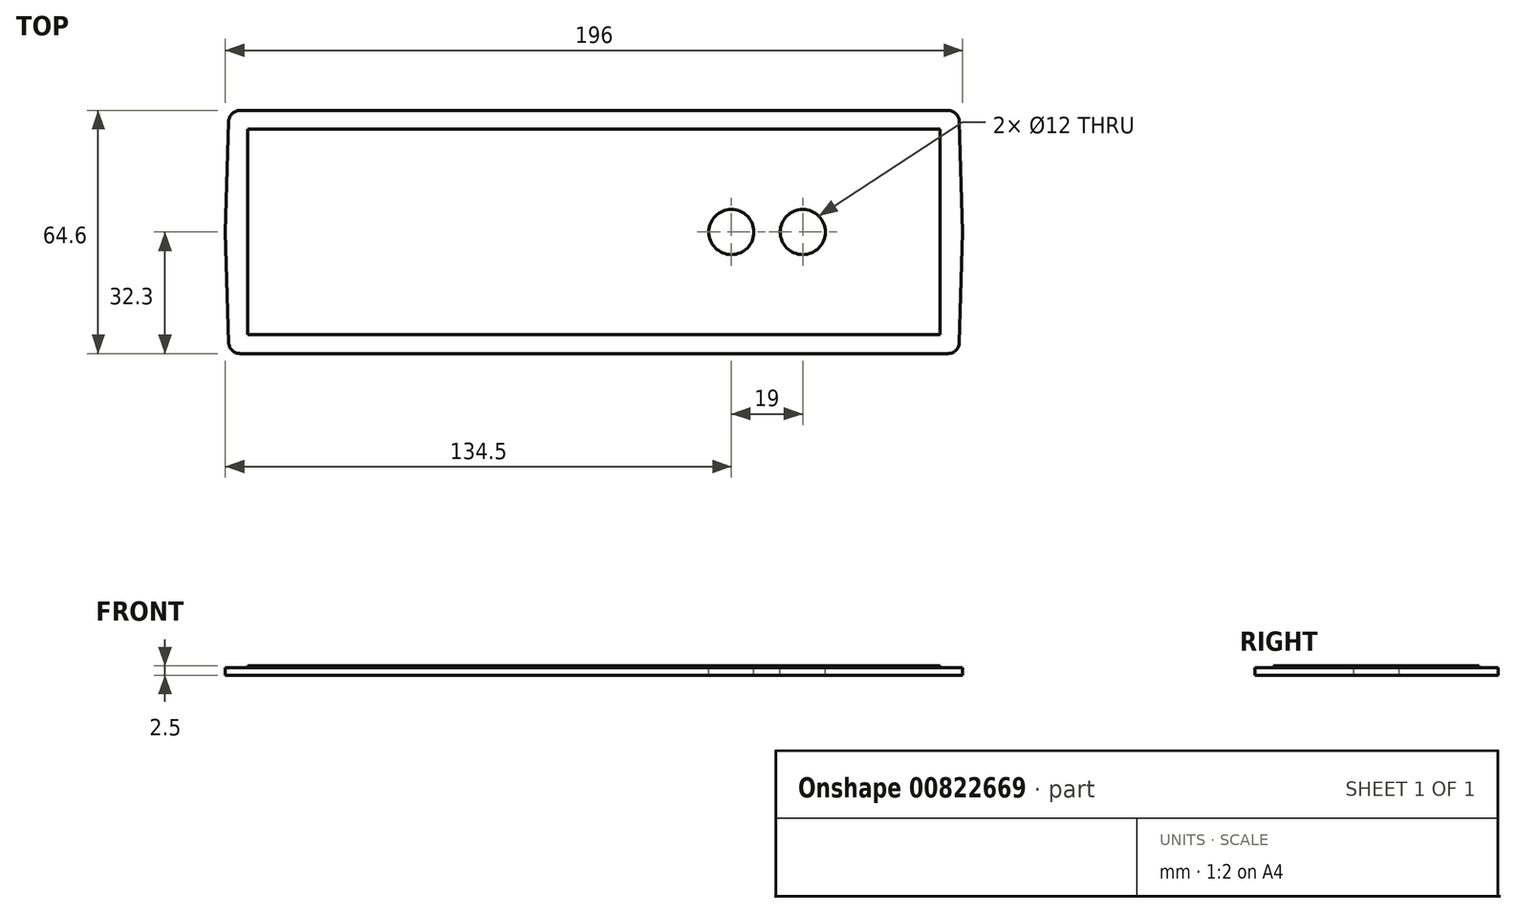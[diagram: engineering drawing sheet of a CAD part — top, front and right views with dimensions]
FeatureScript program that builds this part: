
annotation { "Feature Type Name" : "Feature", "Feature Type Description" : "" }
export const myFeature = defineFeature(function(context is Context, id is Id, definition is map)
    precondition{}
    {
        {
            var Q0;
            Q0=qCreatedBy(makeId("Top.planeOp"),FACE);
            var sketch = newSketch(context, id + "F0", { "sketchPlane" : qUnion([Q0])});
            skLineSegment(sketch, "E0.bottom", {"start": v(97, 32.3) * mm, "end": v(-97, 32.3) * mm});
            skLineSegment(sketch, "E0.top", {"start": v(97, -32.3) * mm, "end": v(-97, -32.3) * mm});
            skLineSegment(sketch, "E0.left", {"start": v(97, 32.3) * mm, "end": v(97, -32.3) * mm});
            skLineSegment(sketch, "E0.right", {"start": v(-97, 32.3) * mm, "end": v(-97, -32.3) * mm});
            skPoint(sketch, "E0.middle", {"position": v(0, 0) * mm});
            skLineSegment(sketch, "E1", {"start": v(98, 0) * mm, "end": v(97, -32.3) * mm});
            skPoint(sketch, "E1.startSnap0", {"position": v(97, 0) * mm});
            skLineSegment(sketch, "E2", {"start": v(98, 0) * mm, "end": v(97, 32.3) * mm});
            skLineSegment(sketch, "E3", {"start": v(-98, 0) * mm, "end": v(-97, 32.3) * mm});
            skLineSegment(sketch, "E4", {"start": v(-98, 0) * mm, "end": v(-97, -32.3) * mm});
            skSolve(sketch);
        }
        {
            var Q0;
            Q0=makeQuery(id+"F0.imprint","IMPRINT",FACE,{"disambiguationData":[TD([[makeQuery(id+"F0.imprint","IMPRINT",EDGE,{"derivedFrom":sQuery(id+"F0.wireOp",EDGE,"E0.bottom")}),1.0]])]});
            var Q1;
            Q1=makeQuery(id+"F0.imprint","IMPRINT",FACE,{"disambiguationData":[TD([[makeQuery(id+"F0.imprint","IMPRINT",EDGE,{"derivedFrom":sQuery(id+"F0.wireOp",EDGE,"E0.left")}),1.0]])]});
            var Q2;
            Q2=makeQuery(id+"F0.imprint","IMPRINT",FACE,{"disambiguationData":[TD([[makeQuery(id+"F0.imprint","IMPRINT",EDGE,{"derivedFrom":sQuery(id+"F0.wireOp",EDGE,"E0.right")}),-1.0]])]});
            extrude(context, id + "F1", {"entities" : qUnion([Q0, Q1, Q2]), "depth" : 2 * mm, "offsetDistance" : 25 * mm});
        }
        {
            var Q0;
            Q0=makeQuery(id+"F1.opExtrude","CAP_FACE",FACE,{"disambiguationData":[OSD([sQuery(id+"F0.wireOp",EDGE,"E0.bottom"),sQuery(id+"F0.wireOp",EDGE,"E0.top"),sQuery(id+"F0.wireOp",EDGE,"E0.left"),sQuery(id+"F0.wireOp",EDGE,"E0.right")])],"isStart":false});
            var sketch = newSketch(context, id + "F2", { "sketchPlane" : qUnion([Q0])});
            skLineSegment(sketch, "E5.bottom", {"start": v(92, 27.3) * mm, "end": v(-92, 27.3) * mm});
            skLineSegment(sketch, "E5.top", {"start": v(92, -27.3) * mm, "end": v(-92, -27.3) * mm});
            skLineSegment(sketch, "E5.left", {"start": v(92, 27.3) * mm, "end": v(92, -27.3) * mm});
            skLineSegment(sketch, "E5.right", {"start": v(-92, 27.3) * mm, "end": v(-92, -27.3) * mm});
            skPoint(sketch, "E5.middle", {"position": v(0, 0) * mm});
            skSolve(sketch);
        }
        {
            var Q0;
            Q0=makeQuery(id+"F2.imprint","IMPRINT",FACE,{"disambiguationData":[TD([[makeQuery(id+"F2.imprint","IMPRINT",EDGE,{"derivedFrom":sQuery(id+"F2.wireOp",EDGE,"E5.bottom")}),1.0]])]});
            extrude(context, id + "F3", {"entities" : qUnion([Q0]), "operationType" : NewBodyOperationType.ADD, "depth" : .5 * mm, "offsetDistance" : 25 * mm});
        }
        {
            var Q0;
            Q0=makeQuery(id+"F3.opExtrude","CAP_FACE",FACE,{"disambiguationData":[OSD([sQuery(id+"F2.wireOp",EDGE,"E5.bottom"),sQuery(id+"F2.wireOp",EDGE,"E5.top"),sQuery(id+"F2.wireOp",EDGE,"E5.left"),sQuery(id+"F2.wireOp",EDGE,"E5.right")])],"isStart":false});
            var sketch = newSketch(context, id + "F4", { "sketchPlane" : qUnion([Q0])});
            skLineSegment(sketch, "E6.bottom", {"start": v(-81.75, 19.75) * mm, "end": v(-10.25, 19.75) * mm});
            skLineSegment(sketch, "E6.top", {"start": v(-81.75, -19.75) * mm, "end": v(-10.25, -19.75) * mm});
            skLineSegment(sketch, "E6.left", {"start": v(-81.75, 19.75) * mm, "end": v(-81.75, -19.75) * mm});
            skLineSegment(sketch, "E6.right", {"start": v(-10.25, 19.75) * mm, "end": v(-10.25, -19.75) * mm});
            skLineSegment(sketch, "E7", {"start": v(-81.75, 19.75) * mm, "end": v(-81.75, 27.3) * mm, "construction": true});
            skLineSegment(sketch, "E8", {"start": v(-81.75, -19.75) * mm, "end": v(-81.75, -27.3) * mm, "construction": true});
            skLineSegment(sketch, "E9", {"start": v(-81.75, 19.75) * mm, "end": v(-92, 19.75) * mm, "construction": true});
            skLineSegment(sketch, "E10", {"start": v(-10.25, 19.75) * mm, "end": v(0, 19.75) * mm, "construction": true});
            skLineSegment(sketch, "E11.bottom", {"start": v(-84.25, 6.37) * mm, "end": v(-79.25, 6.37) * mm});
            skLineSegment(sketch, "E11.top", {"start": v(-84.25, -6.38) * mm, "end": v(-79.25, -6.38) * mm});
            skLineSegment(sketch, "E11.left", {"start": v(-84.25, 6.38) * mm, "end": v(-84.25, -6.38) * mm});
            skLineSegment(sketch, "E11.right", {"start": v(-79.25, 6.38) * mm, "end": v(-79.25, -6.38) * mm});
            skPoint(sketch, "E11.middle", {"position": v(-81.75, 0) * mm});
            skLineSegment(sketch, "E12.bottom", {"start": v(-7.75, 6.37) * mm, "end": v(-12.75, 6.37) * mm});
            skLineSegment(sketch, "E12.top", {"start": v(-7.75, -6.38) * mm, "end": v(-12.75, -6.38) * mm});
            skLineSegment(sketch, "E12.left", {"start": v(-7.75, 6.38) * mm, "end": v(-7.75, -6.38) * mm});
            skLineSegment(sketch, "E12.right", {"start": v(-12.75, 6.38) * mm, "end": v(-12.75, -6.38) * mm});
            skPoint(sketch, "E12.middle", {"position": v(-10.25, 0) * mm});
            skPoint(sketch, "E12.cornerSnap0", {"position": v(-81.75, 6.38) * mm});
            skCircle(sketch, "E13", {"center": v(36.5, 0) * mm, "radius": 6 * mm});
            skCircle(sketch, "E14", {"center": v(55.5, 0) * mm, "radius": 6 * mm});
            skLineSegment(sketch, "E15", {"start": v(36.5, 0) * mm, "end": v(0, 0) * mm, "construction": true});
            skLineSegment(sketch, "E16", {"start": v(55.5, 0) * mm, "end": v(92, 0) * mm, "construction": true});
            skSolve(sketch);
        }
        {
            var Q0;
            Q0=makeQuery(id+"F4.imprint","IMPRINT",FACE,{"disambiguationData":[TD([[makeQuery(id+"F4.imprint","IMPRINT",EDGE,{"derivedFrom":sQuery(id+"F4.wireOp",EDGE,"E13")}),1.0]])]});
            var Q1;
            Q1=makeQuery(id+"F4.imprint","IMPRINT",FACE,{"disambiguationData":[TD([[makeQuery(id+"F4.imprint","IMPRINT",EDGE,{"derivedFrom":sQuery(id+"F4.wireOp",EDGE,"E14")}),1.0]])]});
            extrude(context, id + "F5", {"entities" : qUnion([Q0, Q1]), "operationType" : NewBodyOperationType.REMOVE, "oppositeDirection" : true, "depth" : 25 * mm, "offsetDistance" : 25 * mm});
        }
        {
            var Q0;
            Q0=makeQuery(id+"F1.opExtrude","SWEPT_EDGE",EDGE,{"disambiguationData":[OSD([sQuery(id+"F0.wireOp",EDGE,"E0.top"),sQuery(id+"F0.wireOp",EDGE,"E0.left")])]});
            var Q1;
            Q1=makeQuery(id+"F1.opExtrude","SWEPT_EDGE",EDGE,{"disambiguationData":[OSD([sQuery(id+"F0.wireOp",EDGE,"E0.bottom"),sQuery(id+"F0.wireOp",EDGE,"E0.left")])]});
            var Q2;
            Q2=makeQuery(id+"F1.opExtrude","SWEPT_EDGE",EDGE,{"disambiguationData":[OSD([sQuery(id+"F0.wireOp",EDGE,"E0.bottom"),sQuery(id+"F0.wireOp",EDGE,"E0.right")])]});
            var Q3;
            Q3=makeQuery(id+"F1.opExtrude","SWEPT_EDGE",EDGE,{"disambiguationData":[OSD([sQuery(id+"F0.wireOp",EDGE,"E0.top"),sQuery(id+"F0.wireOp",EDGE,"E0.right")])]});
            var Q4;
            Q4=makeQuery(id+"F1.opExtrude","SWEPT_EDGE",EDGE,{"disambiguationData":[OSD([sQuery(id+"F0.wireOp",EDGE,"E3"),sQuery(id+"F0.wireOp",EDGE,"E4")])]});
            var Q5;
            Q5=makeQuery(id+"F1.opExtrude","SWEPT_EDGE",EDGE,{"disambiguationData":[OSD([sQuery(id+"F0.wireOp",EDGE,"E1"),sQuery(id+"F0.wireOp",EDGE,"E2")])]});
            fillet(context, id + "F6", {"entities" : qUnion([Q0, Q1, Q2, Q3, Q4, Q5]), "radius" : 3 * mm, "tangentPropagation" : true, "allowEdgeOverflow" : false});
        }
    });
